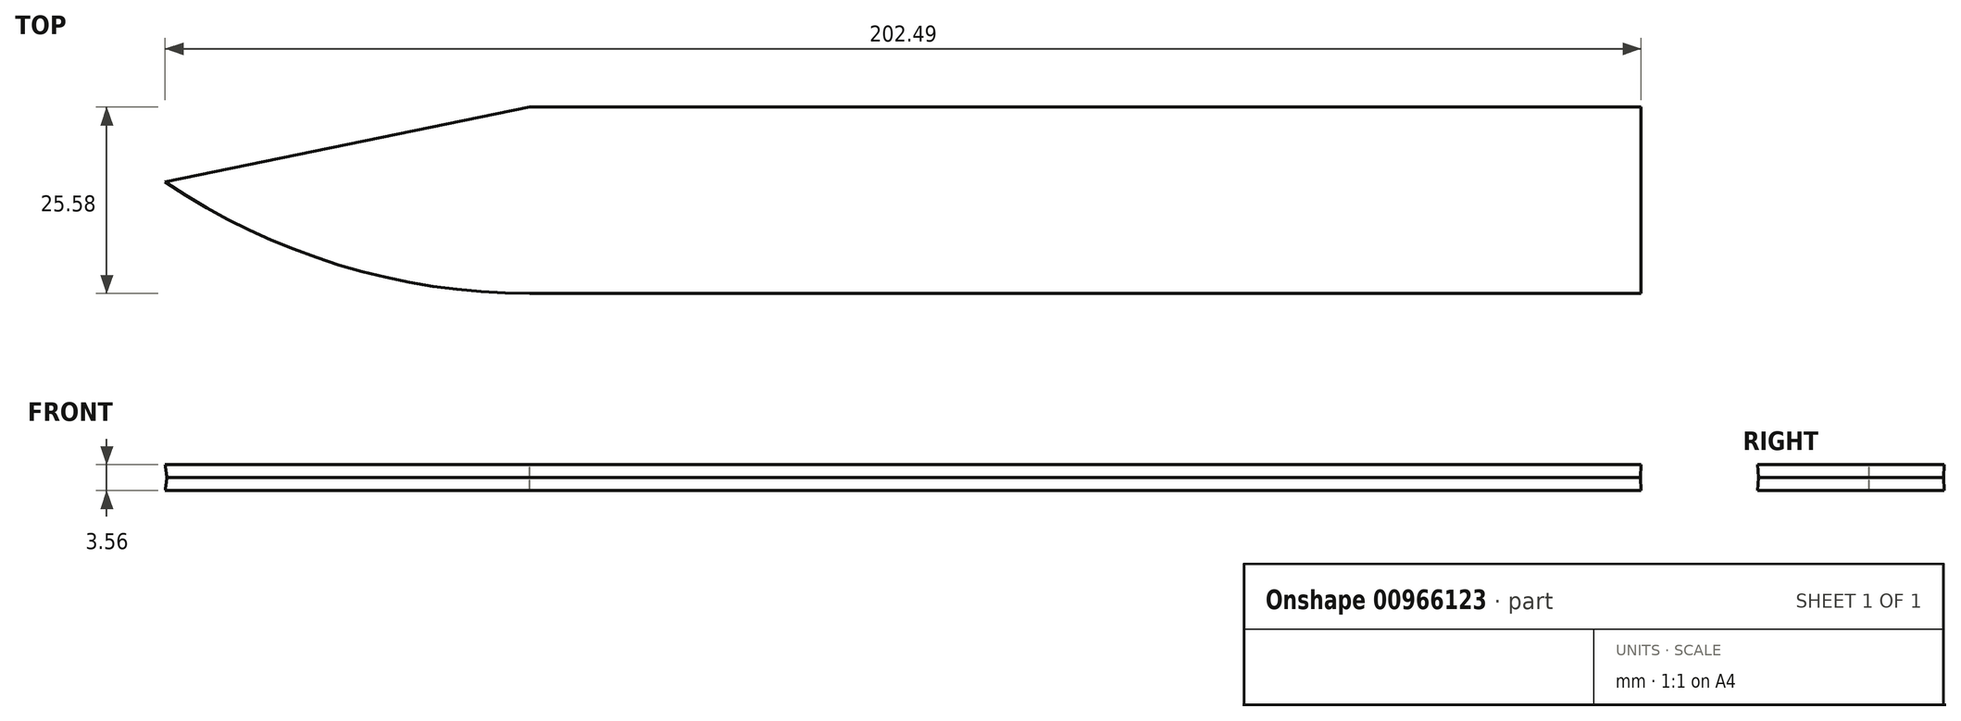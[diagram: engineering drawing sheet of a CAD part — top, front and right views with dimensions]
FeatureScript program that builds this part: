
annotation { "Feature Type Name" : "Feature", "Feature Type Description" : "" }
export const myFeature = defineFeature(function(context is Context, id is Id, definition is map)
    precondition{}
    {
        {
            var Q0;
            Q0=qCreatedBy(makeId("Top.planeOp"),FACE);
            var sketch = newSketch(context, id + "F0", { "sketchPlane" : qUnion([Q0])});
            skLineSegment(sketch, "E0", {"start": v(76.2, 0) * mm, "end": v(-76.2, 0) * mm});
            skLineSegment(sketch, "E1", {"start": v(-76.2, 0) * mm, "end": v(-76.2, 0) * mm});
            skLineSegment(sketch, "E2", {"start": v(-76.2, 0) * mm, "end": v(-125.96, -10.22) * mm});
            skLineSegment(sketch, "E3", {"start": v(-76.2, 0) * mm, "end": v(-76.2, -25.4) * mm});
            skLineSegment(sketch, "E4", {"start": v(76.2, 0) * mm, "end": v(76.2, -25.4) * mm});
            skLineSegment(sketch, "E5", {"start": v(76.2, -25.4) * mm, "end": v(-76.2, -25.4) * mm});
            skArc(sketch, "E6", {"start": v(-125.96, -10.22) * mm, "mid": v(-102.21, -21.52) * mm, "end": v(-76.2, -25.4) * mm});
            skSolve(sketch);
        }
        {
            var Q0;
            Q0 = qSketchRegion(id + "F0", true);
            extrude(context, id + "F1", {"entities" : qUnion([Q0]), "endBound" : BoundingType.SYMMETRIC, "oppositeDirection" : true, "depth" : 3.56 * mm, "offsetDistance" : 25.4 * mm, "hasDraft" : true, "draftAngle" : 3 * degree});
        }
    });
